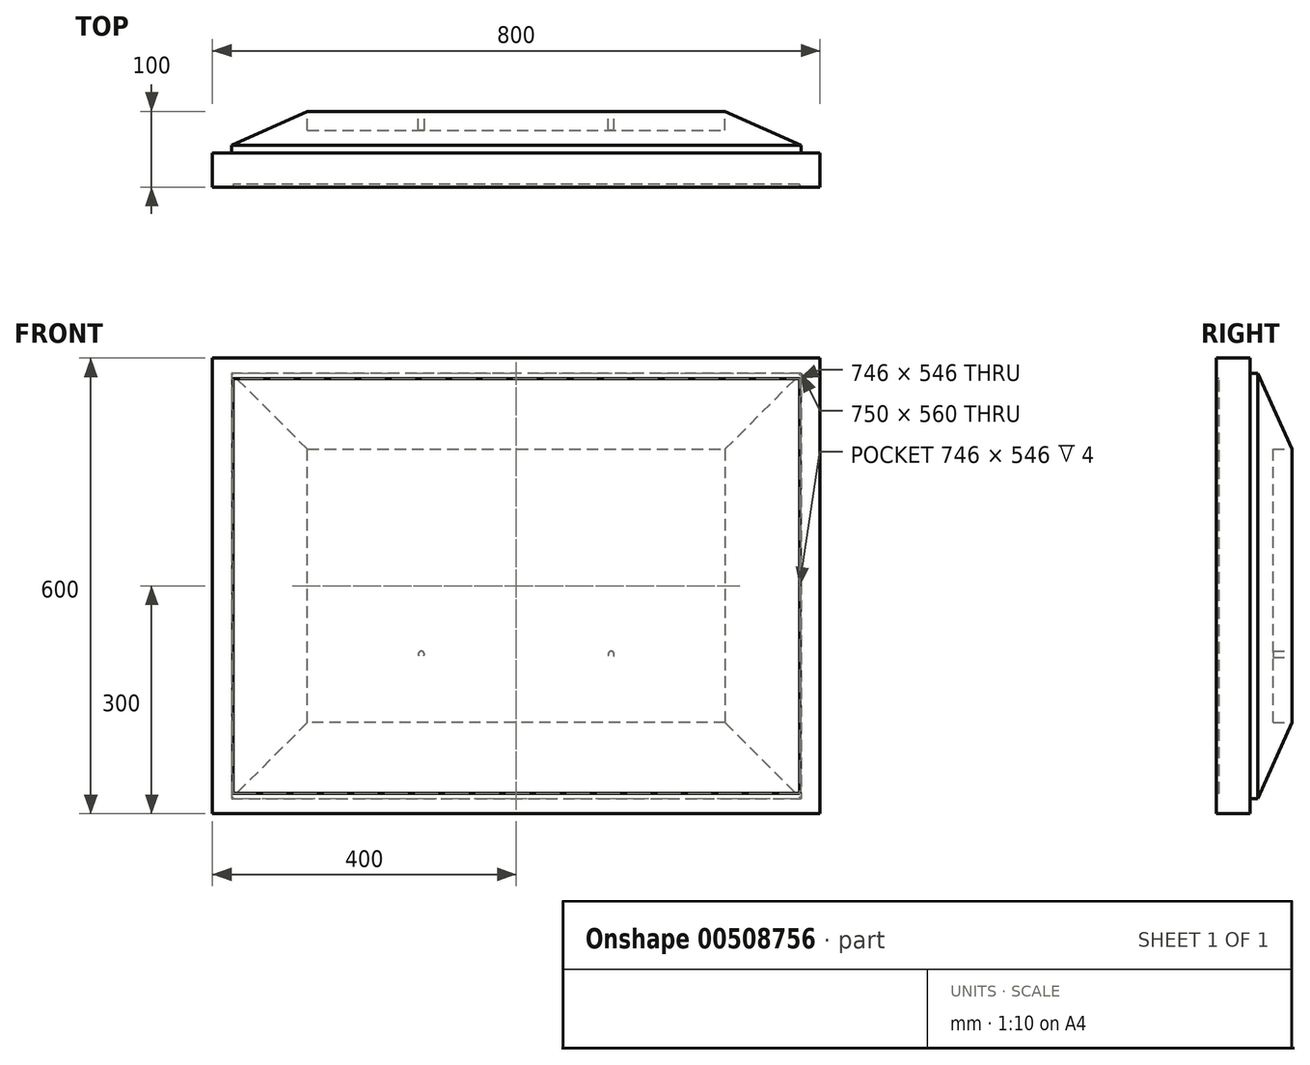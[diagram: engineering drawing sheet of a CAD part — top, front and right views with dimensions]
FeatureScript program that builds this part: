
annotation { "Feature Type Name" : "Feature", "Feature Type Description" : "" }
export const myFeature = defineFeature(function(context is Context, id is Id, definition is map)
    precondition{}
    {
        {
            var Q0;
            Q0=qCreatedBy(makeId("Right.planeOp"),FACE);
            var sketch = newSketch(context, id + "F0", { "sketchPlane" : qUnion([Q0])});
            skLineSegment(sketch, "E0.bottom", {"start": v(-22.5, 300) * mm, "end": v(22.5, 300) * mm});
            skLineSegment(sketch, "E0.top", {"start": v(-22.5, -300) * mm, "end": v(22.5, -300) * mm});
            skLineSegment(sketch, "E0.left", {"start": v(-22.5, 300) * mm, "end": v(-22.5, -300) * mm});
            skLineSegment(sketch, "E0.right", {"start": v(22.5, 300) * mm, "end": v(22.5, -300) * mm});
            skPoint(sketch, "E0.middle", {"position": v(0, 0) * mm});
            skLineSegment(sketch, "E1.bottom", {"start": v(22.5, 280) * mm, "end": v(77.5, 280) * mm});
            skLineSegment(sketch, "E1.top", {"start": v(22.5, -280) * mm, "end": v(77.5, -280) * mm});
            skLineSegment(sketch, "E1.left", {"start": v(22.5, 280) * mm, "end": v(22.5, -280) * mm});
            skLineSegment(sketch, "E1.right", {"start": v(77.5, 280) * mm, "end": v(77.5, -280) * mm});
            skSolve(sketch);
        }
        {
            var Q0;
            {var subQ1=sQuery(id+"F0.wireOp",EDGE,"E0.bottom");Q0=makeQuery(id+"F0.imprint","IMPRINT",FACE,{"disambiguationData":[TD([[makeQuery(id+"F0.imprint","IMPRINT",EDGE,{"derivedFrom":subQ1}),-1.0]])]});}
            var Q1;
            Q1=makeQuery(id+"F0.imprint","IMPRINT",FACE,{"disambiguationData":[TD([[makeQuery(id+"F0.imprint","IMPRINT",EDGE,{"derivedFrom":sQuery(id+"F0.wireOp",EDGE,"E1.bottom")}),-1.0]])]});
            extrude(context, id + "F1", {"entities" : qUnion([Q0, Q1]), "depth" : 800 * mm});
        }
        {
            var Q0;
            Q0=makeQuery(id+"F1.opExtrude","CAP_FACE",FACE,{"disambiguationData":[OSD([sQuery(id+"F0.wireOp",EDGE,"E0.bottom"),sQuery(id+"F0.wireOp",EDGE,"E0.top"),sQuery(id+"F0.wireOp",EDGE,"E0.left"),sQuery(id+"F0.wireOp",EDGE,"E0.right"),sQuery(id+"F0.wireOp",EDGE,"E1.bottom"),sQuery(id+"F0.wireOp",EDGE,"E1.top"),sQuery(id+"F0.wireOp",EDGE,"E1.right")])],"isStart":false});
            var sketch = newSketch(context, id + "F2", { "sketchPlane" : qUnion([Q0])});
            skLineSegment(sketch, "E2.bottom", {"start": v(22.5, 280) * mm, "end": v(77.5, 280) * mm});
            skLineSegment(sketch, "E2.top", {"start": v(22.5, -280) * mm, "end": v(77.5, -280) * mm});
            skLineSegment(sketch, "E2.left", {"start": v(22.5, 280) * mm, "end": v(22.5, -280) * mm});
            skLineSegment(sketch, "E2.right", {"start": v(77.5, 280) * mm, "end": v(77.5, -280) * mm});
            skSolve(sketch);
        }
        {
            var Q0;
            Q0=makeQuery(id+"F2.imprint","IMPRINT",FACE,{"disambiguationData":[TD([[makeQuery(id+"F2.imprint","IMPRINT",EDGE,{"derivedFrom":sQuery(id+"F2.wireOp",EDGE,"E2.bottom")}),-1.0]])]});
            var Q1;
            Q1=makeQuery(id+"F0.imprint","IMPRINT",FACE,{"disambiguationData":[TD([[makeQuery(id+"F0.imprint","IMPRINT",EDGE,{"derivedFrom":sQuery(id+"F0.wireOp",EDGE,"E1.bottom")}),-1.0]])]});
            extrude(context, id + "F3", {"entities" : qUnion([Q0, Q1]), "operationType" : NewBodyOperationType.REMOVE, "endBound" : BoundingType.SYMMETRIC, "oppositeDirection" : true, "depth" : 50 * mm});
        }
        {
            var Q0;
            Q0=makeQuery(id+"F1.opExtrude","SWEPT_FACE",FACE,{"disambiguationData":[OSD([sQuery(id+"F0.wireOp",EDGE,"E1.right")])]});
            chamfer(context, id + "F4", {"entities" : qUnion([Q0]), "chamferType" : ChamferType.TWO_OFFSETS, "width1" : 45 * mm, "oppositeDirection" : false, "width2" : 100 * mm, "tangentPropagation" : true});
        }
        {
            var Q0;
            Q0=makeQuery(id+"F1.opExtrude","SWEPT_FACE",FACE,{"disambiguationData":[OSD([sQuery(id+"F0.wireOp",EDGE,"E0.left")])]});
            var sketch = newSketch(context, id + "F5", { "sketchPlane" : qUnion([Q0])});
            skLineSegment(sketch, "E3.bottom", {"start": v(773, -273) * mm, "end": v(27, -273) * mm});
            skLineSegment(sketch, "E3.top", {"start": v(773, 273) * mm, "end": v(27, 273) * mm});
            skLineSegment(sketch, "E3.left", {"start": v(773, -273) * mm, "end": v(773, 273) * mm});
            skLineSegment(sketch, "E3.right", {"start": v(27, -273) * mm, "end": v(27, 273) * mm});
            skPoint(sketch, "E3.middle", {"position": v(400, 0) * mm});
            skPoint(sketch, "E3.middle.positionSnap0", {"position": v(400, 300) * mm});
            skPoint(sketch, "E3.middle.positionSnap1", {"position": v(0, 0) * mm});
            skPoint(sketch, "E3.centerSnap0", {"position": v(400, 300) * mm});
            skPoint(sketch, "E3.centerSnap1", {"position": v(0, 0) * mm});
            skSolve(sketch);
        }
        {
            var Q0;
            Q0=makeQuery(id+"F5.imprint","IMPRINT",FACE,{"disambiguationData":[TD([[makeQuery(id+"F5.imprint","IMPRINT",EDGE,{"derivedFrom":sQuery(id+"F5.wireOp",EDGE,"E3.bottom")}),-1.0]])]});
            extrude(context, id + "F6", {"entities" : qUnion([Q0]), "operationType" : NewBodyOperationType.REMOVE, "oppositeDirection" : true, "depth" : 4 * mm});
        }
        {
            var Q0;
            Q0=makeQuery(id+"F1.opExtrude","SWEPT_FACE",FACE,{"disambiguationData":[OSD([sQuery(id+"F0.wireOp",EDGE,"E1.right")])]});
            var sketch = newSketch(context, id + "F7", { "sketchPlane" : qUnion([Q0])});
            skLineSegment(sketch, "E4.bottom", {"start": v(-525, -135) * mm, "end": v(-275, -135) * mm});
            skLineSegment(sketch, "E4.top", {"start": v(-525, 135) * mm, "end": v(-275, 135) * mm});
            skLineSegment(sketch, "E4.left", {"start": v(-525, -135) * mm, "end": v(-525, 135) * mm});
            skLineSegment(sketch, "E4.right", {"start": v(-275, -135) * mm, "end": v(-275, 135) * mm});
            skPoint(sketch, "E4.middle", {"position": v(-400, 0) * mm});
            skPoint(sketch, "E4.middle.positionSnap0", {"position": v(-400, 180) * mm});
            skPoint(sketch, "E4.centerSnap0", {"position": v(-400, 180) * mm});
            skCircle(sketch, "E5", {"center": v(-525, 90) * mm, "radius": 4 * mm});
            skCircle(sketch, "E6", {"center": v(-525, -90) * mm, "radius": 4 * mm});
            skCircle(sketch, "E7", {"center": v(-275, -90) * mm, "radius": 4 * mm});
            skCircle(sketch, "E8", {"center": v(-275, 90) * mm, "radius": 4 * mm});
            skSolve(sketch);
        }
        {
            var Q0;
            {var subQ0=sQuery(id+"F7.wireOp",EDGE,"E5");var subQ1=sQuery(id+"F7.wireOp",EDGE,"E4.left");var subQ2=makeQuery(id+"F7.imprint","INTERSECT",VERTEX,{"disambiguationData":[OD(0.0)],"derivedFrom":[subQ1,subQ0]});Q0=makeQuery(id+"F7.imprint","IMPRINT",FACE,{"disambiguationData":[TD([[makeQuery(id+"F7.imprint","IMPRINT",EDGE,{"disambiguationData":[TD([[subQ2,-1.0]])],"derivedFrom":subQ1}),1.0]])]});}
            var Q1;
            {var subQ0=sQuery(id+"F7.wireOp",EDGE,"E5");var subQ1=sQuery(id+"F7.wireOp",EDGE,"E4.left");var subQ2=makeQuery(id+"F7.imprint","INTERSECT",VERTEX,{"disambiguationData":[OD(0.0)],"derivedFrom":[subQ1,subQ0]});Q1=makeQuery(id+"F7.imprint","IMPRINT",FACE,{"disambiguationData":[TD([[makeQuery(id+"F7.imprint","IMPRINT",EDGE,{"disambiguationData":[TD([[subQ2,-1.0]])],"derivedFrom":subQ1}),-1.0]])]});}
            var Q2;
            {var subQ0=sQuery(id+"F7.wireOp",EDGE,"E6");var subQ1=sQuery(id+"F7.wireOp",EDGE,"E4.left");var subQ2=makeQuery(id+"F7.imprint","INTERSECT",VERTEX,{"disambiguationData":[OD(0.0)],"derivedFrom":[subQ1,subQ0]});Q2=makeQuery(id+"F7.imprint","IMPRINT",FACE,{"disambiguationData":[TD([[makeQuery(id+"F7.imprint","IMPRINT",EDGE,{"disambiguationData":[TD([[subQ2,-1.0]])],"derivedFrom":subQ1}),1.0]])]});}
            var Q3;
            {var subQ0=sQuery(id+"F7.wireOp",EDGE,"E6");var subQ1=sQuery(id+"F7.wireOp",EDGE,"E4.left");var subQ2=makeQuery(id+"F7.imprint","INTERSECT",VERTEX,{"disambiguationData":[OD(0.0)],"derivedFrom":[subQ1,subQ0]});Q3=makeQuery(id+"F7.imprint","IMPRINT",FACE,{"disambiguationData":[TD([[makeQuery(id+"F7.imprint","IMPRINT",EDGE,{"disambiguationData":[TD([[subQ2,-1.0]])],"derivedFrom":subQ1}),-1.0]])]});}
            var Q4;
            {var subQ0=sQuery(id+"F7.wireOp",EDGE,"E7");var subQ1=sQuery(id+"F7.wireOp",EDGE,"E4.right");var subQ2=makeQuery(id+"F7.imprint","INTERSECT",VERTEX,{"disambiguationData":[OD(0.0)],"derivedFrom":[subQ1,subQ0]});Q4=makeQuery(id+"F7.imprint","IMPRINT",FACE,{"disambiguationData":[TD([[makeQuery(id+"F7.imprint","IMPRINT",EDGE,{"disambiguationData":[TD([[subQ2,-1.0]])],"derivedFrom":subQ1}),1.0]])]});}
            var Q5;
            {var subQ0=sQuery(id+"F7.wireOp",EDGE,"E7");var subQ1=sQuery(id+"F7.wireOp",EDGE,"E4.right");var subQ2=makeQuery(id+"F7.imprint","INTERSECT",VERTEX,{"disambiguationData":[OD(0.0)],"derivedFrom":[subQ1,subQ0]});Q5=makeQuery(id+"F7.imprint","IMPRINT",FACE,{"disambiguationData":[TD([[makeQuery(id+"F7.imprint","IMPRINT",EDGE,{"disambiguationData":[TD([[subQ2,-1.0]])],"derivedFrom":subQ1}),-1.0]])]});}
            var Q6;
            {var subQ0=sQuery(id+"F7.wireOp",EDGE,"E8");var subQ1=sQuery(id+"F7.wireOp",EDGE,"E4.right");var subQ2=makeQuery(id+"F7.imprint","INTERSECT",VERTEX,{"disambiguationData":[OD(0.0)],"derivedFrom":[subQ1,subQ0]});Q6=makeQuery(id+"F7.imprint","IMPRINT",FACE,{"disambiguationData":[TD([[makeQuery(id+"F7.imprint","IMPRINT",EDGE,{"disambiguationData":[TD([[subQ2,-1.0]])],"derivedFrom":subQ1}),1.0]])]});}
            var Q7;
            {var subQ0=sQuery(id+"F7.wireOp",EDGE,"E8");var subQ1=sQuery(id+"F7.wireOp",EDGE,"E4.right");var subQ2=makeQuery(id+"F7.imprint","INTERSECT",VERTEX,{"disambiguationData":[OD(0.0)],"derivedFrom":[subQ1,subQ0]});Q7=makeQuery(id+"F7.imprint","IMPRINT",FACE,{"disambiguationData":[TD([[makeQuery(id+"F7.imprint","IMPRINT",EDGE,{"disambiguationData":[TD([[subQ2,-1.0]])],"derivedFrom":subQ1}),-1.0]])]});}
            extrude(context, id + "F8", {"entities" : qUnion([Q0, Q1, Q2, Q3, Q4, Q5, Q6, Q7]), "operationType" : NewBodyOperationType.REMOVE, "oppositeDirection" : true, "depth" : 25 * mm});
        }
    });
